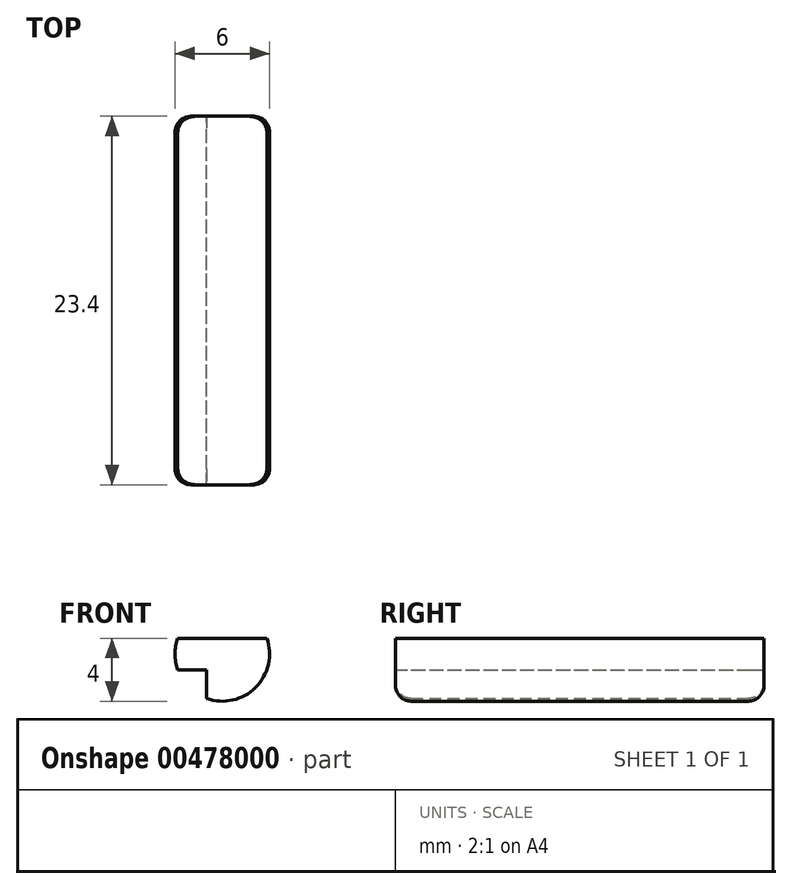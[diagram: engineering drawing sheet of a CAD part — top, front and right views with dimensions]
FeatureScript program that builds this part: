
annotation { "Feature Type Name" : "Feature", "Feature Type Description" : "" }
export const myFeature = defineFeature(function(context is Context, id is Id, definition is map)
    precondition{}
    {
        {
            var Q0;
            Q0=qCreatedBy(makeId("Front.planeOp"),FACE);
            var sketch = newSketch(context, id + "F0", { "sketchPlane" : qUnion([Q0])});
            skCircle(sketch, "E0", {"center": v(13.58, 7.86) * mm, "radius": 3 * mm});
            skLineSegment(sketch, "E1.bottom", {"start": v(14.58, 10.86) * mm, "end": v(12.58, 10.86) * mm});
            skLineSegment(sketch, "E1.top", {"start": v(14.58, 4.86) * mm, "end": v(12.58, 4.86) * mm});
            skLineSegment(sketch, "E1.left", {"start": v(14.58, 10.86) * mm, "end": v(14.58, 4.86) * mm});
            skLineSegment(sketch, "E1.right", {"start": v(12.58, 10.86) * mm, "end": v(12.58, 4.86) * mm});
            skLineSegment(sketch, "E2.bottom", {"start": v(16.58, 8.86) * mm, "end": v(10.58, 8.86) * mm});
            skLineSegment(sketch, "E2.top", {"start": v(16.58, 6.86) * mm, "end": v(10.58, 6.86) * mm});
            skLineSegment(sketch, "E2.left", {"start": v(16.58, 8.86) * mm, "end": v(16.58, 6.86) * mm});
            skLineSegment(sketch, "E2.right", {"start": v(10.58, 8.86) * mm, "end": v(10.58, 6.86) * mm});
            skSolve(sketch);
        }
        {
            var Q0;
            {var subQ0=sQuery(id+"F0.wireOp",EDGE,"E2.bottom");var subQ1=sQuery(id+"F0.wireOp",EDGE,"E0");var subQ2=makeQuery(id+"F0.imprint","INTERSECT",VERTEX,{"disambiguationData":[OD(1.0)],"derivedFrom":[subQ1,subQ0]});Q0=makeQuery(id+"F0.imprint","IMPRINT",FACE,{"disambiguationData":[TD([[makeQuery(id+"F0.imprint","IMPRINT",EDGE,{"disambiguationData":[TD([[subQ2,-1.0]])],"derivedFrom":subQ1}),1.0]])]});}
            var Q1;
            {var subQ0=sQuery(id+"F0.wireOp",EDGE,"E2.bottom");var subQ1=sQuery(id+"F0.wireOp",EDGE,"E1.left");var subQ2=makeQuery(id+"F0.imprint","INTERSECT",VERTEX,{"derivedFrom":[subQ1,subQ0]});Q1=makeQuery(id+"F0.imprint","IMPRINT",FACE,{"disambiguationData":[TD([[makeQuery(id+"F0.imprint","IMPRINT",EDGE,{"disambiguationData":[TD([[subQ2,-1.0]])],"derivedFrom":subQ1}),-1.0]])]});}
            var Q2;
            {var subQ0=sQuery(id+"F0.wireOp",EDGE,"E0");var subQ6=sQuery(id+"F0.wireOp",EDGE,"E1.left");var subQ7=makeQuery(id+"F0.imprint","INTERSECT",VERTEX,{"disambiguationData":[OD(0.0)],"derivedFrom":[subQ0,subQ6]});Q2=makeQuery(id+"F0.imprint","IMPRINT",FACE,{"disambiguationData":[TD([[makeQuery(id+"F0.imprint","IMPRINT",EDGE,{"disambiguationData":[TD([[subQ7,-1.0]])],"derivedFrom":subQ0}),1.0]])]});}
            var Q3;
            {var subQ0=sQuery(id+"F0.wireOp",EDGE,"E1.right");var subQ1=sQuery(id+"F0.wireOp",EDGE,"E0");var subQ2=makeQuery(id+"F0.imprint","INTERSECT",VERTEX,{"disambiguationData":[OD(1.0)],"derivedFrom":[subQ1,subQ0]});Q3=makeQuery(id+"F0.imprint","IMPRINT",FACE,{"disambiguationData":[TD([[makeQuery(id+"F0.imprint","IMPRINT",EDGE,{"disambiguationData":[TD([[subQ2,-1.0]])],"derivedFrom":subQ1}),1.0]])]});}
            var Q4;
            {var subQ0=sQuery(id+"F0.wireOp",EDGE,"E2.bottom");var subQ1=sQuery(id+"F0.wireOp",EDGE,"E0");var subQ2=makeQuery(id+"F0.imprint","INTERSECT",VERTEX,{"disambiguationData":[OD(0.0)],"derivedFrom":[subQ1,subQ0]});Q4=makeQuery(id+"F0.imprint","IMPRINT",FACE,{"disambiguationData":[TD([[makeQuery(id+"F0.imprint","IMPRINT",EDGE,{"disambiguationData":[TD([[subQ2,1.0]])],"derivedFrom":subQ1}),1.0]])]});}
            extrude(context, id + "F1", {"entities" : qUnion([Q0, Q1, Q2, Q3, Q4]), "depth" : 23.4 * mm, "offsetDistance" : 25 * mm});
        }
        {
            var Q0;
            {var subQ0=sQuery(id+"F0.wireOp",EDGE,"E0");var subQ1=makeQuery(id+"F0.imprint","INTERSECT",VERTEX,{"derivedFrom":[subQ0,sQuery(id+"F0.wireOp",EDGE,"E2.left")]});Q0=makeQuery(id+"F1.opExtrude","CAP_EDGE",EDGE,{"disambiguationData":[OSD([subQ0]),TDD([makeQuery(id+"F0.imprint","IMPRINT",EDGE,{"disambiguationData":[TD([[makeQuery(id+"F0.imprint","INTERSECT",VERTEX,{"disambiguationData":[OD(0.0)],"derivedFrom":[subQ0,sQuery(id+"F0.wireOp",EDGE,"E2.bottom")]}),1.0]])],"derivedFrom":subQ0}),makeQuery(id+"F0.imprint","IMPRINT",EDGE,{"disambiguationData":[TD([[subQ1,1.0]])],"derivedFrom":subQ0})])],"isStart":true});}
            var Q1;
            {var subQ0=sQuery(id+"F0.wireOp",EDGE,"E0");var subQ1=makeQuery(id+"F0.imprint","INTERSECT",VERTEX,{"derivedFrom":[subQ0,sQuery(id+"F0.wireOp",EDGE,"E1.bottom")]});Q1=makeQuery(id+"F1.opExtrude","CAP_EDGE",EDGE,{"disambiguationData":[OSD([subQ0]),TDD([makeQuery(id+"F0.imprint","IMPRINT",EDGE,{"disambiguationData":[TD([[makeQuery(id+"F0.imprint","INTERSECT",VERTEX,{"disambiguationData":[OD(0.0)],"derivedFrom":[subQ0,sQuery(id+"F0.wireOp",EDGE,"E1.left")]}),-1.0]])],"derivedFrom":subQ0}),makeQuery(id+"F0.imprint","IMPRINT",EDGE,{"disambiguationData":[TD([[subQ1,-1.0]])],"derivedFrom":subQ0})])],"isStart":true});}
            var Q2;
            {var subQ0=sQuery(id+"F0.wireOp",EDGE,"E0");var subQ1=makeQuery(id+"F0.imprint","INTERSECT",VERTEX,{"derivedFrom":[subQ0,sQuery(id+"F0.wireOp",EDGE,"E2.right")]});Q2=makeQuery(id+"F1.opExtrude","CAP_EDGE",EDGE,{"disambiguationData":[OSD([subQ0]),TDD([makeQuery(id+"F0.imprint","IMPRINT",EDGE,{"disambiguationData":[TD([[makeQuery(id+"F0.imprint","INTERSECT",VERTEX,{"disambiguationData":[OD(1.0)],"derivedFrom":[subQ0,sQuery(id+"F0.wireOp",EDGE,"E2.bottom")]}),-1.0]])],"derivedFrom":subQ0}),makeQuery(id+"F0.imprint","IMPRINT",EDGE,{"disambiguationData":[TD([[subQ1,-1.0]])],"derivedFrom":subQ0})])],"isStart":true});}
            var Q3;
            {var subQ0=sQuery(id+"F0.wireOp",EDGE,"E0");var subQ1=makeQuery(id+"F0.imprint","INTERSECT",VERTEX,{"derivedFrom":[subQ0,sQuery(id+"F0.wireOp",EDGE,"E1.top")]});Q3=makeQuery(id+"F1.opExtrude","CAP_EDGE",EDGE,{"disambiguationData":[OSD([subQ0]),TDD([makeQuery(id+"F0.imprint","IMPRINT",EDGE,{"disambiguationData":[TD([[makeQuery(id+"F0.imprint","INTERSECT",VERTEX,{"disambiguationData":[OD(1.0)],"derivedFrom":[subQ0,sQuery(id+"F0.wireOp",EDGE,"E1.right")]}),-1.0]])],"derivedFrom":subQ0}),makeQuery(id+"F0.imprint","IMPRINT",EDGE,{"disambiguationData":[TD([[subQ1,-1.0]])],"derivedFrom":subQ0})])],"isStart":true});}
            var Q4;
            {var subQ0=sQuery(id+"F0.wireOp",EDGE,"E0");var subQ1=makeQuery(id+"F0.imprint","INTERSECT",VERTEX,{"derivedFrom":[subQ0,sQuery(id+"F0.wireOp",EDGE,"E1.bottom")]});Q4=makeQuery(id+"F1.opExtrude","CAP_EDGE",EDGE,{"disambiguationData":[OSD([subQ0]),TDD([makeQuery(id+"F0.imprint","IMPRINT",EDGE,{"disambiguationData":[TD([[makeQuery(id+"F0.imprint","INTERSECT",VERTEX,{"disambiguationData":[OD(0.0)],"derivedFrom":[subQ0,sQuery(id+"F0.wireOp",EDGE,"E1.left")]}),-1.0]])],"derivedFrom":subQ0}),makeQuery(id+"F0.imprint","IMPRINT",EDGE,{"disambiguationData":[TD([[subQ1,-1.0]])],"derivedFrom":subQ0})])],"isStart":false});}
            var Q5;
            {var subQ0=sQuery(id+"F0.wireOp",EDGE,"E0");var subQ1=makeQuery(id+"F0.imprint","INTERSECT",VERTEX,{"derivedFrom":[subQ0,sQuery(id+"F0.wireOp",EDGE,"E2.right")]});Q5=makeQuery(id+"F1.opExtrude","CAP_EDGE",EDGE,{"disambiguationData":[OSD([subQ0]),TDD([makeQuery(id+"F0.imprint","IMPRINT",EDGE,{"disambiguationData":[TD([[makeQuery(id+"F0.imprint","INTERSECT",VERTEX,{"disambiguationData":[OD(1.0)],"derivedFrom":[subQ0,sQuery(id+"F0.wireOp",EDGE,"E2.bottom")]}),-1.0]])],"derivedFrom":subQ0}),makeQuery(id+"F0.imprint","IMPRINT",EDGE,{"disambiguationData":[TD([[subQ1,-1.0]])],"derivedFrom":subQ0})])],"isStart":false});}
            var Q6;
            {var subQ0=sQuery(id+"F0.wireOp",EDGE,"E0");var subQ1=makeQuery(id+"F0.imprint","INTERSECT",VERTEX,{"derivedFrom":[subQ0,sQuery(id+"F0.wireOp",EDGE,"E1.top")]});Q6=makeQuery(id+"F1.opExtrude","CAP_EDGE",EDGE,{"disambiguationData":[OSD([subQ0]),TDD([makeQuery(id+"F0.imprint","IMPRINT",EDGE,{"disambiguationData":[TD([[makeQuery(id+"F0.imprint","INTERSECT",VERTEX,{"disambiguationData":[OD(1.0)],"derivedFrom":[subQ0,sQuery(id+"F0.wireOp",EDGE,"E1.right")]}),-1.0]])],"derivedFrom":subQ0}),makeQuery(id+"F0.imprint","IMPRINT",EDGE,{"disambiguationData":[TD([[subQ1,-1.0]])],"derivedFrom":subQ0})])],"isStart":false});}
            var Q7;
            {var subQ0=sQuery(id+"F0.wireOp",EDGE,"E0");var subQ1=makeQuery(id+"F0.imprint","INTERSECT",VERTEX,{"derivedFrom":[subQ0,sQuery(id+"F0.wireOp",EDGE,"E2.left")]});Q7=makeQuery(id+"F1.opExtrude","CAP_EDGE",EDGE,{"disambiguationData":[OSD([subQ0]),TDD([makeQuery(id+"F0.imprint","IMPRINT",EDGE,{"disambiguationData":[TD([[makeQuery(id+"F0.imprint","INTERSECT",VERTEX,{"disambiguationData":[OD(0.0)],"derivedFrom":[subQ0,sQuery(id+"F0.wireOp",EDGE,"E2.bottom")]}),1.0]])],"derivedFrom":subQ0}),makeQuery(id+"F0.imprint","IMPRINT",EDGE,{"disambiguationData":[TD([[subQ1,1.0]])],"derivedFrom":subQ0})])],"isStart":false});}
            fillet(context, id + "F2", {"entities" : qUnion([Q0, Q1, Q2, Q3, Q4, Q5, Q6, Q7]), "radius" : 1 * mm, "tangentPropagation" : true, "allowEdgeOverflow" : false});
        }
    });
